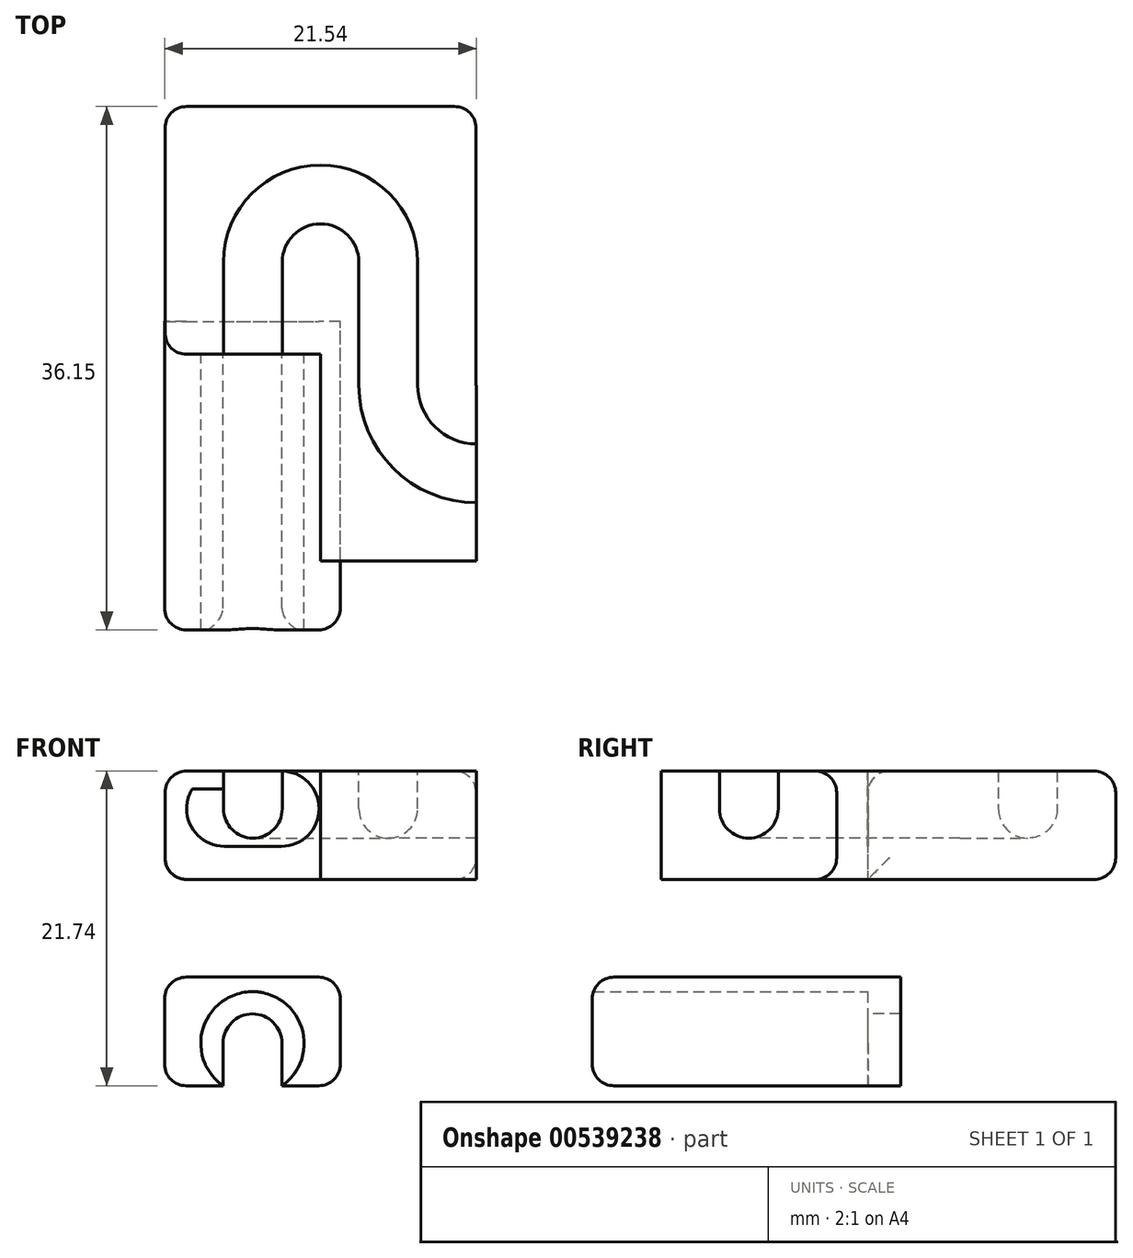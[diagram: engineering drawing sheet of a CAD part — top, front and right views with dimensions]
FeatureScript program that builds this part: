
annotation { "Feature Type Name" : "Feature", "Feature Type Description" : "" }
export const myFeature = defineFeature(function(context is Context, id is Id, definition is map)
    precondition{}
    {
        {
            var Q0;
            Q0=qCreatedBy(makeId("Front.planeOp"),FACE);
            var sketch = newSketch(context, id + "F0", { "sketchPlane" : qUnion([Q0])});
            skLineSegment(sketch, "E0.left", {"start": v(-6.04, 9.8) * mm, "end": v(-6.04, 2.32) * mm});
            skLineSegment(sketch, "E0.right", {"start": v(4.7, 9.8) * mm, "end": v(4.7, 2.32) * mm});
            skLineSegment(sketch, "E1.bottom", {"start": v(-1.94, 4.6) * mm, "end": v(2, 4.6) * mm});
            skArc(sketch, "E2", {"start": v(2, 9.8) * mm, "mid": v(4.6, 7.2) * mm, "end": v(2, 4.6) * mm});
            skArc(sketch, "E3", {"start": v(-1.94, 9.8) * mm, "mid": v(-4.54, 7.2) * mm, "end": v(-1.94, 4.6) * mm});
            skLineSegment(sketch, "E4", {"start": v(-6.04, 2.32) * mm, "end": v(4.7, 2.32) * mm});
            skLineSegment(sketch, "E5", {"start": v(-6.04, 9.8) * mm, "end": v(-1.94, 9.8) * mm});
            skLineSegment(sketch, "E6", {"start": v(2, 9.8) * mm, "end": v(4.7, 9.8) * mm});
            skSolve(sketch);
        }
        {
            var Q0;
            {var subQ1=sQuery(id+"F0.wireOp",EDGE,"E0.left");Q0=makeQuery(id+"F0.imprint","IMPRINT",FACE,{"disambiguationData":[TD([[makeQuery(id+"F0.imprint","IMPRINT",EDGE,{"derivedFrom":subQ1}),1.0]])]});}
            extrude(context, id + "F1", {"entities" : qUnion([Q0]), "depth" : 18 / 812.8 * mm, "offsetDistance" : 25.4 * mm});
        }
        {
            var Q0;
            Q0=qCreatedBy(makeId("Front.planeOp"),FACE);
            var sketch = newSketch(context, id + "F2", { "sketchPlane" : qUnion([Q0])});
            skArc(sketch, "E7", {"start": v(2.03, -11.93) * mm, "mid": v(0, -5.43) * mm, "end": v(-2.03, -11.93) * mm});
            skLineSegment(sketch, "E8", {"start": v(-6.07, -11.93) * mm, "end": v(-2.03, -11.93) * mm});
            skLineSegment(sketch, "E9", {"start": v(2.03, -11.93) * mm, "end": v(6.07, -11.93) * mm});
            skLineSegment(sketch, "E10", {"start": v(-6.07, -11.93) * mm, "end": v(-6.07, -4.43) * mm});
            skLineSegment(sketch, "E11", {"start": v(-6.07, -4.43) * mm, "end": v(6.07, -4.43) * mm});
            skLineSegment(sketch, "E12", {"start": v(6.07, -4.43) * mm, "end": v(6.07, -11.93) * mm});
            skSolve(sketch);
        }
        {
            var Q0;
            Q0 = qSketchRegion(id + "F2", true);
            extrude(context, id + "F3", {"entities" : qUnion([Q0]), "depth" : 19.05 * mm, "offsetDistance" : 25.4 * mm});
        }
        {
            var Q0;
            Q0=makeQuery(id+"F3.opExtrude","CAP_FACE",FACE,{"disambiguationData":[OSD([sQuery(id+"F2.wireOp",EDGE,"E7"),sQuery(id+"F2.wireOp",EDGE,"E8"),sQuery(id+"F2.wireOp",EDGE,"E9"),sQuery(id+"F2.wireOp",EDGE,"E10"),sQuery(id+"F2.wireOp",EDGE,"E11"),sQuery(id+"F2.wireOp",EDGE,"E12")])],"isStart":true});
            var sketch = newSketch(context, id + "F4", { "sketchPlane" : qUnion([Q0])});
            skArc(sketch, "E13", {"start": v(2.03, -9) * mm, "mid": v(0, -6.97) * mm, "end": v(-2.03, -9) * mm});
            skLineSegment(sketch, "E14", {"start": v(-2.03, -9) * mm, "end": v(-2.03, -11.93) * mm});
            skLineSegment(sketch, "E15", {"start": v(-2.03, -11.93) * mm, "end": v(-6.07, -11.93) * mm});
            skLineSegment(sketch, "E16", {"start": v(-6.07, -11.93) * mm, "end": v(-6.07, -4.43) * mm});
            skLineSegment(sketch, "E17", {"start": v(-6.07, -4.43) * mm, "end": v(6.07, -4.43) * mm});
            skLineSegment(sketch, "E18", {"start": v(6.07, -4.43) * mm, "end": v(6.07, -11.93) * mm});
            skLineSegment(sketch, "E19", {"start": v(6.07, -11.93) * mm, "end": v(2.03, -11.93) * mm});
            skLineSegment(sketch, "E20", {"start": v(2.03, -11.93) * mm, "end": v(2.03, -9) * mm});
            skSolve(sketch);
        }
        {
            var Q0;
            Q0 = qSketchRegion(id + "F4", true);
            extrude(context, id + "F5", {"entities" : qUnion([Q0]), "operationType" : NewBodyOperationType.ADD, "depth" : 2.25 * mm, "offsetDistance" : 25.4 * mm});
        }
        {
            var Q0;
            {var subQ1=sQuery(id+"F0.wireOp",EDGE,"E0.left");Q0=makeQuery(id+"F0.imprint","IMPRINT",FACE,{"disambiguationData":[TD([[makeQuery(id+"F0.imprint","IMPRINT",EDGE,{"derivedFrom":subQ1}),1.0]])]});}
            var sketch = newSketch(context, id + "F6", { "sketchPlane" : qUnion([Q0])});
            skLineSegment(sketch, "E21", {"start": v(4.7, 9.8) * mm, "end": v(4.7, 2.32) * mm});
            skLineSegment(sketch, "E22", {"start": v(4.7, 2.32) * mm, "end": v(-6.04, 2.32) * mm});
            skLineSegment(sketch, "E23", {"start": v(-6.04, 2.32) * mm, "end": v(-6.04, 9.8) * mm});
            skArc(sketch, "E24", {"start": v(-2, 7.2) * mm, "mid": v(0.03, 5.17) * mm, "end": v(2.06, 7.2) * mm});
            skLineSegment(sketch, "E25", {"start": v(2.06, 7.2) * mm, "end": v(2.06, 9.8) * mm});
            skLineSegment(sketch, "E26", {"start": v(-2, 7.2) * mm, "end": v(-2, 9.8) * mm});
            skLineSegment(sketch, "E27", {"start": v(4.7, 9.8) * mm, "end": v(2.06, 9.8) * mm});
            skLineSegment(sketch, "E28", {"start": v(-2, 9.8) * mm, "end": v(-6.04, 9.8) * mm});
            skSolve(sketch);
        }
        {
            var Q0;
            Q0 = qSketchRegion(id + "F6", true);
            extrude(context, id + "F7", {"entities" : qUnion([Q0]), "operationType" : NewBodyOperationType.ADD, "oppositeDirection" : true, "depth" : 6.35 * mm, "offsetDistance" : 25.4 * mm});
        }
        {
            var Q0;
            Q0=qCreatedBy(makeId("Top.planeOp"),FACE);
            var sketch = newSketch(context, id + "F8", { "sketchPlane" : qUnion([Q0])});
            skArc(sketch, "E29", {"start": v(9.4, 6.35) * mm, "mid": v(4.7, 11.05) * mm, "end": v(0, 6.35) * mm});
            skLineSegment(sketch, "E30", {"start": v(9.4, 6.35) * mm, "end": v(9.4, -2.15) * mm});
            skArc(sketch, "E31", {"start": v(9.4, -2.15) * mm, "mid": v(11.18, -6.44) * mm, "end": v(15.47, -8.22) * mm});
            skSolve(sketch);
        }
        {
            var Q0;
            Q0=makeQuery(id+"F7.opExtrude","CAP_FACE",FACE,{"disambiguationData":[OSD([sQuery(id+"F6.wireOp",EDGE,"E21"),sQuery(id+"F6.wireOp",EDGE,"E22"),sQuery(id+"F6.wireOp",EDGE,"E23"),sQuery(id+"F6.wireOp",EDGE,"E24"),sQuery(id+"F6.wireOp",EDGE,"E25"),sQuery(id+"F6.wireOp",EDGE,"E26"),sQuery(id+"F6.wireOp",EDGE,"E27"),sQuery(id+"F6.wireOp",EDGE,"E28")])],"isStart":false});
            var Q1;
            Q1=sQuery(id+"F8.wireOp",EDGE,"S1vB0Hbf-tFia-fncB-AK3D-2OWwRvvrkEQq");
            var Q2;
            Q2=sQuery(id+"F8.wireOp",EDGE,"E29");
            var Q3;
            Q3=sQuery(id+"F8.wireOp",EDGE,"E30");
            var Q4;
            Q4=sQuery(id+"F8.wireOp",EDGE,"E31");
            sweep(context, id + "F9", {"operationType" : NewBodyOperationType.ADD, "profiles" : qUnion([Q0]), "path" : qUnion([Q1, Q2, Q3, Q4])});
        }
        {
            var Q0;
            {var subQ0=sQuery(id+"F0.wireOp",EDGE,"E0.bottom");Q0=makeQuery(id+"F9.boolean.opBoolean","MERGE",FACE,{"derivedFrom":[makeQuery(id+"F1.opExtrude","SWEPT_FACE",FACE,{"disambiguationData":[OSD([subQ0]),TDD([makeQuery(id+"F0.imprint","IMPRINT",EDGE,{"disambiguationData":[TD([[makeQuery(id+"F0.imprint","INTERSECT",VERTEX,{"derivedFrom":[subQ0,sQuery(id+"F0.wireOp",EDGE,"E0.left")]}),-1.0]])],"derivedFrom":subQ0})])]}),makeQuery(id+"F9.opSweep","SWEPT_FACE",FACE,{"disambiguationData":[OSD([sQuery(id+"F6.wireOp",EDGE,"E28"),sQuery(id+"F8.wireOp",EDGE,"S1vB0Hbf-tFia-fncB-AK3D-2OWwRvvrkEQq")])]})]});}
            var sketch = newSketch(context, id + "F10", { "sketchPlane" : qUnion([Q0])});
            skLineSegment(sketch, "E32", {"start": v(4.7, -14.29) * mm, "end": v(15.47, -14.29) * mm});
            skLineSegment(sketch, "E33", {"start": v(15.47, -14.29) * mm, "end": v(15.47, -12.92) * mm});
            skLineSegment(sketch, "E34", {"start": v(4.7, 6.35) * mm, "end": v(4.7, -14.29) * mm});
            skLineSegment(sketch, "E35", {"start": v(4.7, 6.35) * mm, "end": v(4.7, 6.35) * mm});
            skLineSegment(sketch, "E36", {"start": v(4.7, 6.35) * mm, "end": v(4.7, -2.15) * mm});
            skArc(sketch, "E37", {"start": v(4.7, -2.15) * mm, "mid": v(7.86, -9.76) * mm, "end": v(15.47, -12.92) * mm});
            skLineSegment(sketch, "E38", {"start": v(-6.04, 6.35) * mm, "end": v(-6.04, 17.1) * mm});
            skLineSegment(sketch, "E39", {"start": v(-6.04, 17.1) * mm, "end": v(15.45, 17.1) * mm});
            skPoint(sketch, "E39.endSnap0", {"position": v(4.7, 17.1) * mm});
            skLineSegment(sketch, "E40", {"start": v(15.45, 17.1) * mm, "end": v(15.45, 6.35) * mm});
            skSolve(sketch);
        }
        {
            var Q0;
            Q0 = qSketchRegion(id + "F10", true);
            var Q1;
            {var subQ0=sQuery(id+"F10.wireOp",EDGE,"E38");Q1=makeQuery(id+"F10.imprint","IMPRINT",FACE,{"disambiguationData":[TD([[makeQuery(id+"F10.imprint","IMPRINT",EDGE,{"derivedFrom":subQ0}),-1.0]])]});}
            var Q2;
            {var subQ0=sQuery(id+"F10.wireOp",EDGE,"E40");Q2=makeQuery(id+"F10.imprint","IMPRINT",FACE,{"disambiguationData":[TD([[makeQuery(id+"F10.imprint","IMPRINT",EDGE,{"derivedFrom":subQ0}),-1.0]])]});}
            extrude(context, id + "F11", {"entities" : qUnion([Q0, Q1, Q2]), "operationType" : NewBodyOperationType.ADD, "oppositeDirection" : true, "depth" : 7.5 * mm, "offsetDistance" : 25.4 * mm});
        }
        {
            var Q0;
            Q0=makeQuery(id+"F1.opExtrude","CAP_EDGE",EDGE,{"disambiguationData":[OSD([sQuery(id+"F0.wireOp",EDGE,"E0.left")])],"isStart":false});
            var Q1;
            Q1=makeQuery(id+"F11.boolean.opBoolean","MERGE",EDGE,{"derivedFrom":[makeQuery(id+"F1.opExtrude","CAP_EDGE",EDGE,{"disambiguationData":[OSD([sQuery(id+"F0.wireOp",EDGE,"E4")])],"isStart":false}),makeQuery(id+"F11.opExtrude","CAP_EDGE",EDGE,{"disambiguationData":[OSD([sQuery(id+"F10.wireOp",EDGE,"E32")])],"isStart":false})]});
            var Q2;
            {var subQ0=sQuery(id+"F0.wireOp",EDGE,"E0.bottom");Q2=makeQuery(id+"F11.boolean.opBoolean","MERGE",EDGE,{"derivedFrom":[makeQuery(id+"F1.opExtrude","CAP_EDGE",EDGE,{"disambiguationData":[OSD([subQ0]),TDD([makeQuery(id+"F0.imprint","IMPRINT",EDGE,{"disambiguationData":[TD([[makeQuery(id+"F0.imprint","INTERSECT",VERTEX,{"derivedFrom":[subQ0,sQuery(id+"F0.wireOp",EDGE,"E0.right")]}),1.0]])],"derivedFrom":subQ0})])],"isStart":false}),makeQuery(id+"F11.opExtrude","CAP_EDGE",EDGE,{"disambiguationData":[OSD([sQuery(id+"F10.wireOp",EDGE,"E32")])],"isStart":true})]});}
            var Q3;
            Q3=makeQuery(id+"F5.boolean.opBoolean","MERGE",EDGE,{"derivedFrom":[makeQuery(id+"F3.opExtrude","SWEPT_EDGE",EDGE,{"disambiguationData":[OSD([sQuery(id+"F2.wireOp",EDGE,"E8"),sQuery(id+"F2.wireOp",EDGE,"E10")])]}),makeQuery(id+"F5.opExtrude","SWEPT_EDGE",EDGE,{"disambiguationData":[OSD([sQuery(id+"F4.wireOp",EDGE,"E18"),sQuery(id+"F4.wireOp",EDGE,"E19")])]})]});
            var Q4;
            Q4=makeQuery(id+"F3.opExtrude","CAP_EDGE",EDGE,{"disambiguationData":[OSD([sQuery(id+"F2.wireOp",EDGE,"E10")])],"isStart":false});
            var Q5;
            Q5=makeQuery(id+"F3.opExtrude","CAP_EDGE",EDGE,{"disambiguationData":[OSD([sQuery(id+"F2.wireOp",EDGE,"E12")])],"isStart":false});
            var Q6;
            Q6=makeQuery(id+"F5.boolean.opBoolean","MERGE",EDGE,{"derivedFrom":[makeQuery(id+"F3.opExtrude","SWEPT_EDGE",EDGE,{"disambiguationData":[OSD([sQuery(id+"F2.wireOp",EDGE,"E11"),sQuery(id+"F2.wireOp",EDGE,"E12")])]}),makeQuery(id+"F5.opExtrude","SWEPT_EDGE",EDGE,{"disambiguationData":[OSD([sQuery(id+"F4.wireOp",EDGE,"E16"),sQuery(id+"F4.wireOp",EDGE,"E17")])]})]});
            var Q7;
            Q7=makeQuery(id+"F3.opExtrude","CAP_EDGE",EDGE,{"disambiguationData":[OSD([sQuery(id+"F2.wireOp",EDGE,"E11")])],"isStart":false});
            var Q8;
            Q8=makeQuery(id+"F5.boolean.opBoolean","MERGE",EDGE,{"derivedFrom":[makeQuery(id+"F3.opExtrude","SWEPT_EDGE",EDGE,{"disambiguationData":[OSD([sQuery(id+"F2.wireOp",EDGE,"E10"),sQuery(id+"F2.wireOp",EDGE,"E11")])]}),makeQuery(id+"F5.opExtrude","SWEPT_EDGE",EDGE,{"disambiguationData":[OSD([sQuery(id+"F4.wireOp",EDGE,"E17"),sQuery(id+"F4.wireOp",EDGE,"E18")])]})]});
            var Q9;
            Q9=makeQuery(id+"F5.boolean.opBoolean","MERGE",EDGE,{"derivedFrom":[makeQuery(id+"F3.opExtrude","SWEPT_EDGE",EDGE,{"disambiguationData":[OSD([sQuery(id+"F2.wireOp",EDGE,"E9"),sQuery(id+"F2.wireOp",EDGE,"E12")])]}),makeQuery(id+"F5.opExtrude","SWEPT_EDGE",EDGE,{"disambiguationData":[OSD([sQuery(id+"F4.wireOp",EDGE,"E15"),sQuery(id+"F4.wireOp",EDGE,"E16")])]})]});
            var Q10;
            Q10=makeQuery(id+"F11.boolean.opBoolean","MERGE",EDGE,{"derivedFrom":[makeQuery(id+"F9.opSweep","SWEPT_EDGE",EDGE,{"disambiguationData":[OSD([sQuery(id+"F6.wireOp",EDGE,"E23"),sQuery(id+"F6.wireOp",EDGE,"E28"),sQuery(id+"F8.wireOp",EDGE,"E30")])]}),makeQuery(id+"F11.opExtrude","CAP_EDGE",EDGE,{"disambiguationData":[OSD([sQuery(id+"F10.wireOp",EDGE,"eC3eoRWE-6scv-WGwV-pHR3-kdHLMxEgUBIk")])],"isStart":true})]});
            var Q11;
            Q11=makeQuery(id+"F11.boolean.opBoolean","MERGE",EDGE,{"derivedFrom":[makeQuery(id+"F9.opSweep","SWEPT_EDGE",EDGE,{"disambiguationData":[OSD([sQuery(id+"F6.wireOp",EDGE,"E22"),sQuery(id+"F6.wireOp",EDGE,"E23"),sQuery(id+"F8.wireOp",EDGE,"E30")])]}),makeQuery(id+"F11.opExtrude","CAP_EDGE",EDGE,{"disambiguationData":[OSD([sQuery(id+"F10.wireOp",EDGE,"eC3eoRWE-6scv-WGwV-pHR3-kdHLMxEgUBIk")])],"isStart":false})]});
            var Q12;
            Q12=makeQuery(id+"F7.opExtrude","SWEPT_EDGE",EDGE,{"disambiguationData":[OSD([sQuery(id+"F6.wireOp",EDGE,"E23"),sQuery(id+"F6.wireOp",EDGE,"E28")])]});
            var Q13;
            Q13=makeQuery(id+"F7.opExtrude","SWEPT_EDGE",EDGE,{"disambiguationData":[OSD([sQuery(id+"F6.wireOp",EDGE,"E22"),sQuery(id+"F6.wireOp",EDGE,"E23")])]});
            var Q14;
            {var subQ0=sQuery(id+"F10.wireOp",EDGE,"E39");Q14=makeQuery(id+"F11.boolean.opBoolean","MERGE",EDGE,{"derivedFrom":[makeQuery(id+"F11.opExtrude","CAP_EDGE",EDGE,{"disambiguationData":[OSD([subQ0]),TDD([makeQuery(id+"F10.imprint","IMPRINT",EDGE,{"disambiguationData":[TD([[makeQuery(id+"F10.imprint","INTERSECT",VERTEX,{"derivedFrom":[sQuery(id+"F10.wireOp",EDGE,"E38"),subQ0]}),-1.0]])],"derivedFrom":subQ0})])],"isStart":false}),makeQuery(id+"F11.opExtrude","CAP_EDGE",EDGE,{"disambiguationData":[OSD([subQ0]),TDD([makeQuery(id+"F10.imprint","IMPRINT",EDGE,{"disambiguationData":[TD([[makeQuery(id+"F10.imprint","INTERSECT",VERTEX,{"derivedFrom":[subQ0,sQuery(id+"F10.wireOp",EDGE,"E40")]}),1.0]])],"derivedFrom":subQ0})])],"isStart":false})]});}
            var Q15;
            Q15=makeQuery(id+"F11.opExtrude","SWEPT_EDGE",EDGE,{"disambiguationData":[OSD([sQuery(id+"F10.wireOp",EDGE,"E38"),sQuery(id+"F10.wireOp",EDGE,"E39")])]});
            var Q16;
            {var subQ0=sQuery(id+"F10.wireOp",EDGE,"E39");Q16=makeQuery(id+"F11.boolean.opBoolean","MERGE",EDGE,{"derivedFrom":[makeQuery(id+"F11.opExtrude","CAP_EDGE",EDGE,{"disambiguationData":[OSD([subQ0]),TDD([makeQuery(id+"F10.imprint","IMPRINT",EDGE,{"disambiguationData":[TD([[makeQuery(id+"F10.imprint","INTERSECT",VERTEX,{"derivedFrom":[sQuery(id+"F10.wireOp",EDGE,"E38"),subQ0]}),-1.0]])],"derivedFrom":subQ0})])],"isStart":true}),makeQuery(id+"F11.opExtrude","CAP_EDGE",EDGE,{"disambiguationData":[OSD([subQ0]),TDD([makeQuery(id+"F10.imprint","IMPRINT",EDGE,{"disambiguationData":[TD([[makeQuery(id+"F10.imprint","INTERSECT",VERTEX,{"derivedFrom":[subQ0,sQuery(id+"F10.wireOp",EDGE,"E40")]}),1.0]])],"derivedFrom":subQ0})])],"isStart":true})]});}
            var Q17;
            Q17=makeQuery(id+"F11.opExtrude","SWEPT_EDGE",EDGE,{"disambiguationData":[OSD([sQuery(id+"F10.wireOp",EDGE,"E39"),sQuery(id+"F10.wireOp",EDGE,"E40")])]});
            var Q18;
            Q18=makeQuery(id+"F1.opExtrude","CAP_EDGE",EDGE,{"disambiguationData":[OSD([sQuery(id+"F0.wireOp",EDGE,"E5")])],"isStart":false});
            var Q19;
            Q19=makeQuery(id+"F3.opExtrude","CAP_EDGE",EDGE,{"disambiguationData":[OSD([sQuery(id+"F2.wireOp",EDGE,"E8")])],"isStart":false});
            var Q20;
            Q20=makeQuery(id+"F3.opExtrude","CAP_EDGE",EDGE,{"disambiguationData":[OSD([sQuery(id+"F2.wireOp",EDGE,"E9")])],"isStart":false});
            fillet(context, id + "F12", {"entities" : qUnion([Q0, Q1, Q2, Q3, Q4, Q5, Q6, Q7, Q8, Q9, Q10, Q11, Q12, Q13, Q14, Q15, Q16, Q17, Q18, Q19, Q20]), "radius" : 1.5 * mm, "tangentPropagation" : true, "allowEdgeOverflow" : false});
        }
    });
